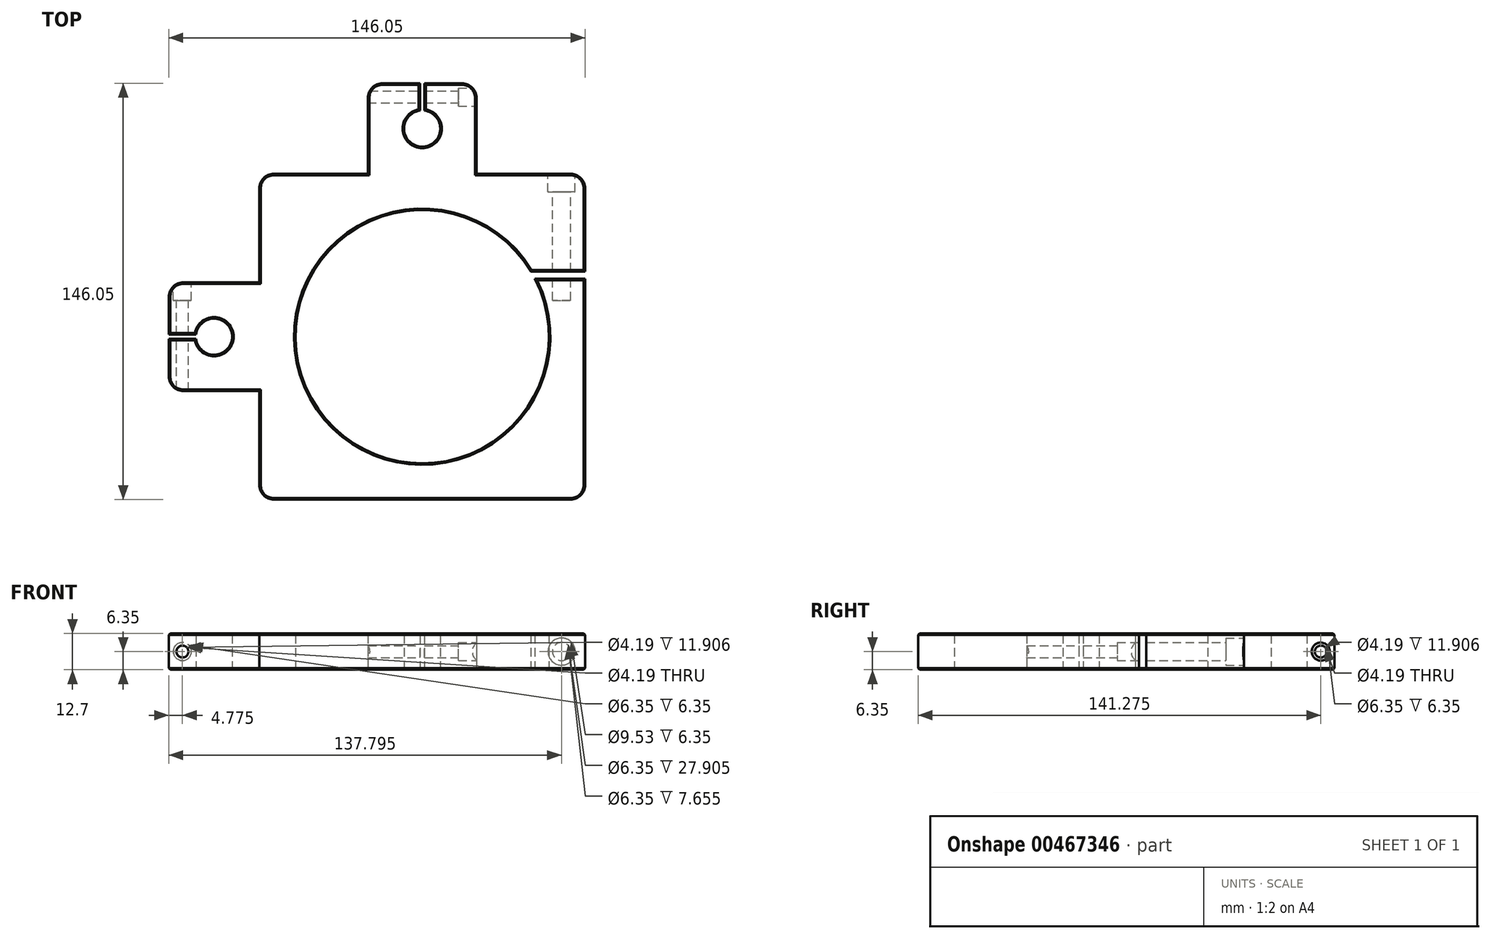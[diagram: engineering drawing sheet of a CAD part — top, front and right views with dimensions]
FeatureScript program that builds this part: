
annotation { "Feature Type Name" : "Feature", "Feature Type Description" : "" }
export const myFeature = defineFeature(function(context is Context, id is Id, definition is map)
    precondition{}
    {
        {
            var Q0;
            Q0=qCreatedBy(makeId("Top.planeOp"),FACE);
            var sketch = newSketch(context, id + "F0", { "sketchPlane" : qUnion([Q0])});
            skLineSegment(sketch, "E0.bottom", {"start": v(57.15, 57.15) * mm, "end": v(19.05, 57.15) * mm});
            skLineSegment(sketch, "E0.top", {"start": v(57.15, -57.15) * mm, "end": v(-57.15, -57.15) * mm});
            skLineSegment(sketch, "E0.left", {"start": v(57.15, 57.15) * mm, "end": v(57.15, 22.9) * mm});
            skLineSegment(sketch, "E0.right", {"start": v(-57.15, 57.15) * mm, "end": v(-57.15, 19.05) * mm});
            skPoint(sketch, "E0.middle", {"position": v(0, 0) * mm});
            skArc(sketch, "E1", {"start": v(38.1, 22.9) * mm, "mid": v(-38.83, -21.64) * mm, "end": v(39.52, 20.36) * mm});
            skLineSegment(sketch, "E2.bottom", {"start": v(-88.9, 19.05) * mm, "end": v(-57.15, 19.05) * mm});
            skLineSegment(sketch, "E2.top", {"start": v(-88.9, -19.05) * mm, "end": v(-57.15, -19.05) * mm});
            skLineSegment(sketch, "E2.left", {"start": v(-88.9, 19.05) * mm, "end": v(-88.9, 0.8) * mm});
            skLineSegment(sketch, "E3.bottom", {"start": v(19.05, 88.9) * mm, "end": v(0.8, 88.9) * mm});
            skLineSegment(sketch, "E3.left", {"start": v(19.05, 88.9) * mm, "end": v(19.05, 57.15) * mm});
            skLineSegment(sketch, "E3.right", {"start": v(-19.05, 88.9) * mm, "end": v(-19.05, 57.15) * mm});
            skPoint(sketch, "E3.middle", {"position": v(0, 57.15) * mm});
            skLineSegment(sketch, "E4.trimOffspring", {"start": v(-57.15, -19.05) * mm, "end": v(-57.15, -57.15) * mm});
            skLineSegment(sketch, "E5.trimOffspring", {"start": v(-19.05, 57.15) * mm, "end": v(-57.15, 57.15) * mm});
            skLineSegment(sketch, "E6", {"start": v(0, -57.15) * mm, "end": v(0, 88.9) * mm, "construction": true});
            skLineSegment(sketch, "E7", {"start": v(-88.9, 0) * mm, "end": v(57.15, 0) * mm, "construction": true});
            skLineSegment(sketch, "E8", {"start": v(-19.05, 57.15) * mm, "end": v(19.05, 57.15) * mm, "construction": true});
            skLineSegment(sketch, "E9", {"start": v(-57.15, 19.05) * mm, "end": v(-57.15, -19.05) * mm, "construction": true});
            skLineSegment(sketch, "E10", {"start": v(-19.05, 57.15) * mm, "end": v(19.05, 88.9) * mm, "construction": true});
            skLineSegment(sketch, "E11", {"start": v(-19.05, 88.9) * mm, "end": v(19.05, 57.15) * mm, "construction": true});
            skLineSegment(sketch, "E12", {"start": v(-88.9, 19.05) * mm, "end": v(-57.15, -19.05) * mm, "construction": true});
            skLineSegment(sketch, "E13", {"start": v(-57.15, 19.05) * mm, "end": v(-88.9, -19.05) * mm, "construction": true});
            skArc(sketch, "E14", {"start": v(-79.33, -0.8) * mm, "mid": v(-66.68, 0) * mm, "end": v(-79.33, 0.8) * mm});
            skArc(sketch, "E15", {"start": v(-0.8, 79.33) * mm, "mid": v(0, 66.68) * mm, "end": v(0.8, 79.33) * mm});
            skPoint(sketch, "E16.visualSharp", {"position": v(57.15, 57.15) * mm});
            skLineSegment(sketch, "E16.filletArc", {"start": v(57.15, 57.15) * mm, "end": v(57.15, 57.15) * mm});
            skPoint(sketch, "E17.visualSharp", {"position": v(57.15, -57.15) * mm});
            skLineSegment(sketch, "E17.filletArc", {"start": v(57.15, -57.15) * mm, "end": v(57.15, -57.15) * mm});
            skPoint(sketch, "E18.visualSharp", {"position": v(-57.15, -57.15) * mm});
            skLineSegment(sketch, "E18.filletArc", {"start": v(-57.15, -57.15) * mm, "end": v(-57.15, -57.15) * mm});
            skPoint(sketch, "E19.visualSharp", {"position": v(-88.9, 19.05) * mm});
            skPoint(sketch, "E20.visualSharp", {"position": v(-88.9, -19.05) * mm});
            skPoint(sketch, "E21.visualSharp", {"position": v(-19.05, 88.9) * mm});
            skPoint(sketch, "E22.visualSharp", {"position": v(19.05, 88.9) * mm});
            skLineSegment(sketch, "E23.left", {"start": v(0.8, 88.9) * mm, "end": v(0.8, 79.33) * mm});
            skLineSegment(sketch, "E23.right", {"start": v(-0.8, 88.9) * mm, "end": v(-0.8, 79.33) * mm});
            skLineSegment(sketch, "E24.bottom", {"start": v(-88.9, 0.8) * mm, "end": v(-79.33, 0.8) * mm});
            skLineSegment(sketch, "E24.top", {"start": v(-88.9, -0.8) * mm, "end": v(-79.33, -0.8) * mm});
            skLineSegment(sketch, "E25.trimOffspring", {"start": v(-88.9, -0.8) * mm, "end": v(-88.9, -19.05) * mm});
            skLineSegment(sketch, "E26.trimOffspring", {"start": v(-0.8, 88.9) * mm, "end": v(-19.05, 88.9) * mm});
            skLineSegment(sketch, "E27.bottom", {"start": v(38.1, 22.9) * mm, "end": v(57.15, 22.9) * mm});
            skLineSegment(sketch, "E27.top", {"start": v(39.52, 20.36) * mm, "end": v(57.15, 20.36) * mm});
            skLineSegment(sketch, "E28.trimOffspring", {"start": v(57.15, 20.36) * mm, "end": v(57.15, -57.15) * mm});
            skSolve(sketch);
        }
        {
            var Q0;
            Q0=makeQuery(id+"F0.imprint","IMPRINT",FACE,{"disambiguationData":[TD([[makeQuery(id+"F0.imprint","IMPRINT",EDGE,{"derivedFrom":sQuery(id+"F0.wireOp",EDGE,"E0.bottom")}),1.0]])]});
            extrude(context, id + "F1", {"entities" : qUnion([Q0]), "depth" : 12.7 * mm});
        }
        {
            var Q0;
            Q0=makeQuery(id+"F1.opExtrude","SWEPT_FACE",FACE,{"disambiguationData":[OSD([sQuery(id+"F0.wireOp",EDGE,"E3.left")])]});
            var sketch = newSketch(context, id + "F2", { "sketchPlane" : qUnion([Q0])});
            skCircle(sketch, "E29", {"center": v(84.12, 6.35) * mm, "radius": 2.1 * mm});
            skCircle(sketch, "E30", {"center": v(84.12, 6.35) * mm, "radius": 3.18 * mm});
            skPoint(sketch, "E31.start.orphan", {"position": v(57.15, 6.35) * mm});
            skSolve(sketch);
        }
        {
            var Q0;
            Q0=makeQuery(id+"F2.imprint","IMPRINT",FACE,{"disambiguationData":[TD([[makeQuery(id+"F2.imprint","IMPRINT",EDGE,{"derivedFrom":sQuery(id+"F2.wireOp",EDGE,"E29")}),1.0]])]});
            extrude(context, id + "F3", {"entities" : qUnion([Q0]), "operationType" : NewBodyOperationType.REMOVE, "endBound" : BoundingType.THROUGH_ALL, "oppositeDirection" : true, "depth" : 25.4 * mm});
        }
        {
            var Q0;
            {var subQ0=sQuery(id+"F2.wireOp",EDGE,"E30");var subQ1=makeQuery(id+"F1.opExtrude","SWEPT_EDGE",EDGE,{"disambiguationData":[OSD([sQuery(id+"F0.wireOp",EDGE,"E3.left"),sQuery(id+"F0.wireOp",EDGE,"E22.filletArc")])]});var subQ2=makeQuery(id+"F2.imprint","INTERSECT",VERTEX,{"disambiguationData":[OD(0.0)],"derivedFrom":[subQ1,subQ0]});Q0=makeQuery(id+"F2.imprint","IMPRINT",FACE,{"disambiguationData":[TD([[makeQuery(id+"F2.imprint","IMPRINT",EDGE,{"disambiguationData":[TD([[subQ2,1.0]])],"derivedFrom":subQ0}),1.0]])]});}
            extrude(context, id + "F4", {"entities" : qUnion([Q0]), "operationType" : NewBodyOperationType.REMOVE, "oppositeDirection" : true, "depth" : 6.35 * mm});
        }
        {
            var Q0;
            Q0=makeQuery(id+"F2.imprint","IMPRINT",FACE,{"disambiguationData":[TD([[makeQuery(id+"F2.imprint","IMPRINT",EDGE,{"derivedFrom":sQuery(id+"F2.wireOp",EDGE,"E29")}),-1.0]])]});
            extrude(context, id + "F5", {"entities" : qUnion([Q0]), "operationType" : NewBodyOperationType.REMOVE, "oppositeDirection" : true, "depth" : 6.35 * mm});
        }
        {
            var Q0;
            Q0=makeQuery(id+"F1.opExtrude","SWEPT_FACE",FACE,{"disambiguationData":[OSD([sQuery(id+"F0.wireOp",EDGE,"E2.bottom")])]});
            var sketch = newSketch(context, id + "F6", { "sketchPlane" : qUnion([Q0])});
            skCircle(sketch, "E32", {"center": v(84.12, 6.35) * mm, "radius": 2.1 * mm});
            skCircle(sketch, "E33", {"center": v(84.12, 6.35) * mm, "radius": 3.18 * mm});
            skSolve(sketch);
        }
        {
            var Q0;
            {var subQ0=sQuery(id+"F6.wireOp",EDGE,"E32");var subQ1=makeQuery(id+"F1.opExtrude","SWEPT_EDGE",EDGE,{"disambiguationData":[OSD([sQuery(id+"F0.wireOp",EDGE,"E2.bottom"),sQuery(id+"F0.wireOp",EDGE,"E19.filletArc")])]});var subQ2=makeQuery(id+"F6.imprint","INTERSECT",VERTEX,{"disambiguationData":[OD(0.0)],"derivedFrom":[subQ1,subQ0]});Q0=makeQuery(id+"F6.imprint","IMPRINT",FACE,{"disambiguationData":[TD([[makeQuery(id+"F6.imprint","IMPRINT",EDGE,{"disambiguationData":[TD([[subQ2,1.0]])],"derivedFrom":subQ0}),1.0]])]});}
            var Q1;
            Q1=sQuery(id+"F6.wireOp",EDGE,"E32");
            extrude(context, id + "F7", {"entities" : qUnion([Q0]), "operationType" : NewBodyOperationType.REMOVE, "surfaceEntities" : qUnion([Q1]), "endBound" : BoundingType.THROUGH_ALL, "oppositeDirection" : true, "depth" : 25.4 * mm});
        }
        {
            var Q0;
            {var subQ0=sQuery(id+"F6.wireOp",EDGE,"E32");var subQ1=makeQuery(id+"F1.opExtrude","SWEPT_EDGE",EDGE,{"disambiguationData":[OSD([sQuery(id+"F0.wireOp",EDGE,"E2.bottom"),sQuery(id+"F0.wireOp",EDGE,"E19.filletArc")])]});var subQ2=makeQuery(id+"F6.imprint","INTERSECT",VERTEX,{"disambiguationData":[OD(0.0)],"derivedFrom":[subQ1,subQ0]});Q0=makeQuery(id+"F6.imprint","IMPRINT",FACE,{"disambiguationData":[TD([[makeQuery(id+"F6.imprint","IMPRINT",EDGE,{"disambiguationData":[TD([[subQ2,-1.0]])],"derivedFrom":subQ0}),1.0]])]});}
            extrude(context, id + "F8", {"entities" : qUnion([Q0]), "operationType" : NewBodyOperationType.REMOVE, "endBound" : BoundingType.THROUGH_ALL, "oppositeDirection" : true, "depth" : 25.4 * mm});
        }
        {
            var Q0;
            {var subQ0=sQuery(id+"F6.wireOp",EDGE,"E32");var subQ1=makeQuery(id+"F1.opExtrude","SWEPT_EDGE",EDGE,{"disambiguationData":[OSD([sQuery(id+"F0.wireOp",EDGE,"E2.bottom"),sQuery(id+"F0.wireOp",EDGE,"E19.filletArc")])]});var subQ2=makeQuery(id+"F6.imprint","INTERSECT",VERTEX,{"disambiguationData":[OD(0.0)],"derivedFrom":[subQ1,subQ0]});Q0=makeQuery(id+"F6.imprint","IMPRINT",FACE,{"disambiguationData":[TD([[makeQuery(id+"F6.imprint","IMPRINT",EDGE,{"disambiguationData":[TD([[subQ2,1.0]])],"derivedFrom":subQ0}),-1.0]])]});}
            extrude(context, id + "F9", {"entities" : qUnion([Q0]), "operationType" : NewBodyOperationType.REMOVE, "oppositeDirection" : true, "depth" : 6.35 * mm});
        }
        {
            var Q0;
            {var subQ0=sQuery(id+"F6.wireOp",EDGE,"E32");var subQ1=makeQuery(id+"F1.opExtrude","SWEPT_EDGE",EDGE,{"disambiguationData":[OSD([sQuery(id+"F0.wireOp",EDGE,"E2.bottom"),sQuery(id+"F0.wireOp",EDGE,"E19.filletArc")])]});var subQ2=makeQuery(id+"F6.imprint","INTERSECT",VERTEX,{"disambiguationData":[OD(0.0)],"derivedFrom":[subQ1,subQ0]});Q0=makeQuery(id+"F6.imprint","IMPRINT",FACE,{"disambiguationData":[TD([[makeQuery(id+"F6.imprint","IMPRINT",EDGE,{"disambiguationData":[TD([[subQ2,-1.0]])],"derivedFrom":subQ0}),-1.0]])]});}
            extrude(context, id + "F10", {"entities" : qUnion([Q0]), "operationType" : NewBodyOperationType.REMOVE, "oppositeDirection" : true, "depth" : 6.35 * mm});
        }
        {
            var Q0;
            Q0=makeQuery(id+"F1.opExtrude","SWEPT_FACE",FACE,{"disambiguationData":[OSD([sQuery(id+"F0.wireOp",EDGE,"E0.bottom")])]});
            var sketch = newSketch(context, id + "F11", { "sketchPlane" : qUnion([Q0])});
            skCircle(sketch, "E34", {"center": v(-48.9, 6.35) * mm, "radius": 3.18 * mm});
            skCircle(sketch, "E35", {"center": v(-48.9, 6.35) * mm, "radius": 4.76 * mm});
            skSolve(sketch);
        }
        {
            var Q0;
            {var subQ0=sQuery(id+"F11.wireOp",EDGE,"E34");var subQ1=makeQuery(id+"F1.opExtrude","SWEPT_EDGE",EDGE,{"disambiguationData":[OSD([sQuery(id+"F0.wireOp",EDGE,"E0.bottom"),sQuery(id+"F0.wireOp",EDGE,"E16.filletArc")])]});var subQ2=makeQuery(id+"F11.imprint","INTERSECT",VERTEX,{"disambiguationData":[OD(0.0)],"derivedFrom":[subQ1,subQ0]});Q0=makeQuery(id+"F11.imprint","IMPRINT",FACE,{"disambiguationData":[TD([[makeQuery(id+"F11.imprint","IMPRINT",EDGE,{"disambiguationData":[TD([[subQ2,1.0]])],"derivedFrom":subQ0}),-1.0]])]});}
            var Q1;
            {var subQ0=sQuery(id+"F11.wireOp",EDGE,"E34");var subQ1=makeQuery(id+"F1.opExtrude","SWEPT_EDGE",EDGE,{"disambiguationData":[OSD([sQuery(id+"F0.wireOp",EDGE,"E0.bottom"),sQuery(id+"F0.wireOp",EDGE,"E16.filletArc")])]});var subQ2=makeQuery(id+"F11.imprint","INTERSECT",VERTEX,{"disambiguationData":[OD(0.0)],"derivedFrom":[subQ1,subQ0]});Q1=makeQuery(id+"F11.imprint","IMPRINT",FACE,{"disambiguationData":[TD([[makeQuery(id+"F11.imprint","IMPRINT",EDGE,{"disambiguationData":[TD([[subQ2,-1.0]])],"derivedFrom":subQ0}),-1.0]])]});}
            extrude(context, id + "F12", {"entities" : qUnion([Q0, Q1]), "operationType" : NewBodyOperationType.REMOVE, "oppositeDirection" : true, "depth" : 6.35 * mm});
        }
        {
            var Q0;
            Q0=makeQuery(id+"F12.boolean.opBoolean","SPLIT",FACE,{"disambiguationData":[TD([makeQuery(id+"F12.opExtrude","SWEPT_FACE",FACE,{"disambiguationData":[OSD([sQuery(id+"F11.wireOp",EDGE,"E34")])]})])],"derivedFrom":makeQuery(id+"F1.opExtrude","SWEPT_FACE",FACE,{"disambiguationData":[OSD([sQuery(id+"F0.wireOp",EDGE,"E0.bottom")])]})});
            extrude(context, id + "F13", {"entities" : qUnion([Q0]), "operationType" : NewBodyOperationType.REMOVE, "oppositeDirection" : true, "depth" : 44.45 * mm});
        }
        {
            var Q0;
            Q0=makeQuery(id+"F1.opExtrude","SWEPT_EDGE",EDGE,{"disambiguationData":[OSD([sQuery(id+"F0.wireOp",EDGE,"E0.bottom"),sQuery(id+"F0.wireOp",EDGE,"E0.left")])]});
            var Q1;
            Q1=makeQuery(id+"F1.opExtrude","SWEPT_EDGE",EDGE,{"disambiguationData":[OSD([sQuery(id+"F0.wireOp",EDGE,"E0.top"),sQuery(id+"F0.wireOp",EDGE,"E28.trimOffspring")])]});
            var Q2;
            Q2=makeQuery(id+"F1.opExtrude","SWEPT_EDGE",EDGE,{"disambiguationData":[OSD([sQuery(id+"F0.wireOp",EDGE,"E0.top"),sQuery(id+"F0.wireOp",EDGE,"E4.trimOffspring")])]});
            var Q3;
            Q3=makeQuery(id+"F1.opExtrude","SWEPT_EDGE",EDGE,{"disambiguationData":[OSD([sQuery(id+"F0.wireOp",EDGE,"E0.right"),sQuery(id+"F0.wireOp",EDGE,"E5.trimOffspring")])]});
            var Q4;
            Q4=makeQuery(id+"F1.opExtrude","SWEPT_EDGE",EDGE,{"disambiguationData":[OSD([sQuery(id+"F0.wireOp",EDGE,"E0.bottom"),sQuery(id+"F0.wireOp",EDGE,"E0.left")])]});
            var Q5;
            Q5=makeQuery(id+"F1.opExtrude","SWEPT_EDGE",EDGE,{"disambiguationData":[OSD([sQuery(id+"F0.wireOp",EDGE,"E2.bottom"),sQuery(id+"F0.wireOp",EDGE,"E2.left")])]});
            var Q6;
            Q6=makeQuery(id+"F1.opExtrude","SWEPT_EDGE",EDGE,{"disambiguationData":[OSD([sQuery(id+"F0.wireOp",EDGE,"E2.top"),sQuery(id+"F0.wireOp",EDGE,"E25.trimOffspring")])]});
            var Q7;
            Q7=makeQuery(id+"F1.opExtrude","SWEPT_EDGE",EDGE,{"disambiguationData":[OSD([sQuery(id+"F0.wireOp",EDGE,"E0.top"),sQuery(id+"F0.wireOp",EDGE,"E4.trimOffspring")])]});
            var Q8;
            Q8=makeQuery(id+"F1.opExtrude","SWEPT_EDGE",EDGE,{"disambiguationData":[OSD([sQuery(id+"F0.wireOp",EDGE,"E3.right"),sQuery(id+"F0.wireOp",EDGE,"E26.trimOffspring")])]});
            var Q9;
            Q9=makeQuery(id+"F1.opExtrude","SWEPT_EDGE",EDGE,{"disambiguationData":[OSD([sQuery(id+"F0.wireOp",EDGE,"E3.bottom"),sQuery(id+"F0.wireOp",EDGE,"E3.left")])]});
            fillet(context, id + "F14", {"entities" : qUnion([Q0, Q1, Q2, Q3, Q4, Q5, Q6, Q7, Q8, Q9]), "radius" : 5.08 * mm, "tangentPropagation" : true, "allowEdgeOverflow" : false});
        }
        {
            var Q0;
            Q0=makeQuery(id+"F1.opExtrude","CAP_FACE",FACE,{"disambiguationData":[OSD([sQuery(id+"F0.wireOp",EDGE,"E0.bottom"),sQuery(id+"F0.wireOp",EDGE,"E0.top"),sQuery(id+"F0.wireOp",EDGE,"E0.left"),sQuery(id+"F0.wireOp",EDGE,"E0.right"),sQuery(id+"F0.wireOp",EDGE,"E1"),sQuery(id+"F0.wireOp",EDGE,"E2.bottom"),sQuery(id+"F0.wireOp",EDGE,"E2.top"),sQuery(id+"F0.wireOp",EDGE,"E2.left"),sQuery(id+"F0.wireOp",EDGE,"E3.bottom"),sQuery(id+"F0.wireOp",EDGE,"E3.left"),sQuery(id+"F0.wireOp",EDGE,"E3.right"),sQuery(id+"F0.wireOp",EDGE,"E4.trimOffspring"),sQuery(id+"F0.wireOp",EDGE,"E5.trimOffspring"),sQuery(id+"F0.wireOp",EDGE,"E14"),sQuery(id+"F0.wireOp",EDGE,"E15"),sQuery(id+"F0.wireOp",EDGE,"E23.left"),sQuery(id+"F0.wireOp",EDGE,"E23.right"),sQuery(id+"F0.wireOp",EDGE,"E24.bottom"),sQuery(id+"F0.wireOp",EDGE,"E24.top"),sQuery(id+"F0.wireOp",EDGE,"E25.trimOffspring"),sQuery(id+"F0.wireOp",EDGE,"E26.trimOffspring"),sQuery(id+"F0.wireOp",EDGE,"E27.bottom"),sQuery(id+"F0.wireOp",EDGE,"E27.top"),sQuery(id+"F0.wireOp",EDGE,"E28.trimOffspring")])],"isStart":false});
            var Q1;
            Q1=makeQuery(id+"F1.opExtrude","CAP_FACE",FACE,{"disambiguationData":[OSD([sQuery(id+"F0.wireOp",EDGE,"E0.bottom"),sQuery(id+"F0.wireOp",EDGE,"E0.top"),sQuery(id+"F0.wireOp",EDGE,"E0.left"),sQuery(id+"F0.wireOp",EDGE,"E0.right"),sQuery(id+"F0.wireOp",EDGE,"E1"),sQuery(id+"F0.wireOp",EDGE,"E2.bottom"),sQuery(id+"F0.wireOp",EDGE,"E2.top"),sQuery(id+"F0.wireOp",EDGE,"E2.left"),sQuery(id+"F0.wireOp",EDGE,"E3.bottom"),sQuery(id+"F0.wireOp",EDGE,"E3.left"),sQuery(id+"F0.wireOp",EDGE,"E3.right"),sQuery(id+"F0.wireOp",EDGE,"E4.trimOffspring"),sQuery(id+"F0.wireOp",EDGE,"E5.trimOffspring"),sQuery(id+"F0.wireOp",EDGE,"E14"),sQuery(id+"F0.wireOp",EDGE,"E15"),sQuery(id+"F0.wireOp",EDGE,"E23.left"),sQuery(id+"F0.wireOp",EDGE,"E23.right"),sQuery(id+"F0.wireOp",EDGE,"E24.bottom"),sQuery(id+"F0.wireOp",EDGE,"E24.top"),sQuery(id+"F0.wireOp",EDGE,"E25.trimOffspring"),sQuery(id+"F0.wireOp",EDGE,"E26.trimOffspring"),sQuery(id+"F0.wireOp",EDGE,"E27.bottom"),sQuery(id+"F0.wireOp",EDGE,"E27.top"),sQuery(id+"F0.wireOp",EDGE,"E28.trimOffspring")])],"isStart":true});
            chamfer(context, id + "F15", {"entities" : qUnion([Q0, Q1]), "width" : 0.5 * mm, "tangentPropagation" : true});
        }
    });
